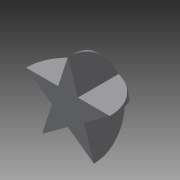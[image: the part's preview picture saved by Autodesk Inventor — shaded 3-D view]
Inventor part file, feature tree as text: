
AUTODESK INVENTOR PART (.ipt)
format: ipt  version: 2013 (Build 170138000, 138)  size: 96,768 bytes
history: native  units: mm
features: sketch x2, other x1, revolve x1, extrude x1
ambient origin geometry x8: Origin, YZ Plane, XZ Plane, XY Plane, X Axis, Y Axis, Z Axis, Center Point
feature tree (5):
  other  "ソリッド1"
  revolve  "回転1"
  extrude  "押し出し2"  Depth=26.0mm
  sketch  "スケッチ1"
  sketch  "スケッチ3"
